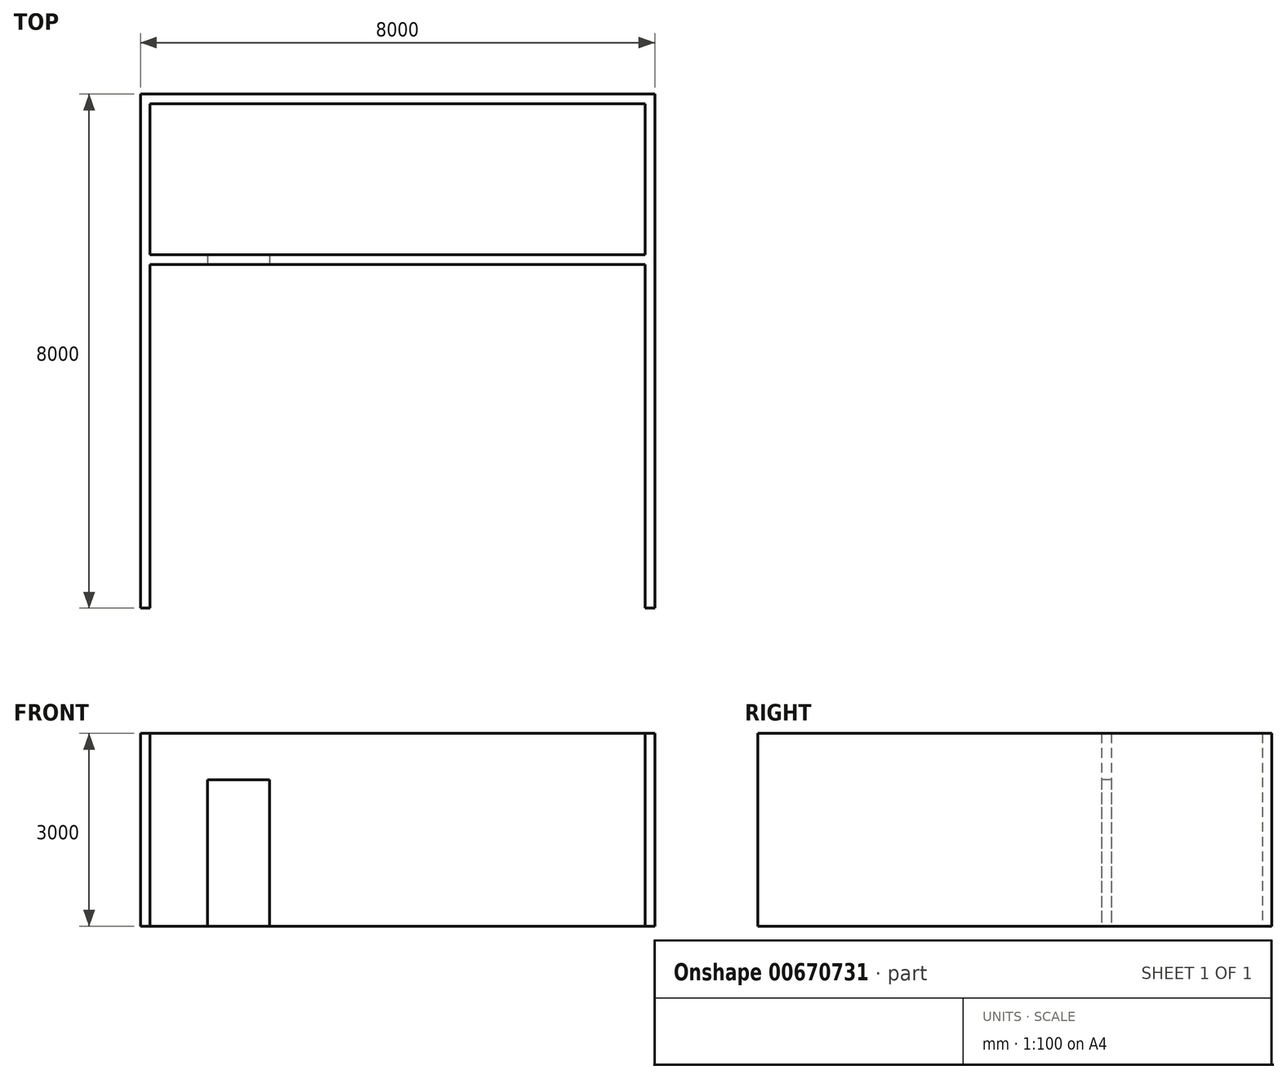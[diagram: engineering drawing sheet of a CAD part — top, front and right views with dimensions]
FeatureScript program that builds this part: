
annotation { "Feature Type Name" : "Feature", "Feature Type Description" : "" }
export const myFeature = defineFeature(function(context is Context, id is Id, definition is map)
    precondition{}
    {
        {
            var Q0;
            Q0=qCreatedBy(makeId("Top.planeOp"),FACE);
            var sketch = newSketch(context, id + "F0", { "sketchPlane" : qUnion([Q0])});
            skLineSegment(sketch, "E0.bottom", {"start": v(4000, 4000) * mm, "end": v(-4000, 4000) * mm});
            skLineSegment(sketch, "E0.top", {"start": v(4000, -4000) * mm, "end": v(3850, -4000) * mm});
            skLineSegment(sketch, "E0.left", {"start": v(4000, 4000) * mm, "end": v(4000, -4000) * mm});
            skLineSegment(sketch, "E0.right", {"start": v(-4000, 4000) * mm, "end": v(-4000, -4000) * mm});
            skPoint(sketch, "E0.middle", {"position": v(0, 0) * mm});
            skLineSegment(sketch, "E1.0", {"start": v(-3850, 3850) * mm, "end": v(-3850, -4000) * mm});
            skLineSegment(sketch, "E1.1", {"start": v(3850, 3850) * mm, "end": v(-3850, 3850) * mm});
            skLineSegment(sketch, "E1.2", {"start": v(3850, 3850) * mm, "end": v(3850, -4000) * mm});
            skLineSegment(sketch, "E2.bottom", {"start": v(-3850, 1500) * mm, "end": v(3850, 1500) * mm});
            skLineSegment(sketch, "E2.top", {"start": v(-3850, 1350) * mm, "end": v(3850, 1350) * mm});
            skLineSegment(sketch, "E2.left", {"start": v(-3850, 1500) * mm, "end": v(-3850, 1350) * mm});
            skLineSegment(sketch, "E2.right", {"start": v(3850, 1500) * mm, "end": v(3850, 1350) * mm});
            skLineSegment(sketch, "E3.trimOffspring", {"start": v(-3850, -4000) * mm, "end": v(-4000, -4000) * mm});
            skSolve(sketch);
        }
        {
            var Q0;
            Q0 = qSketchRegion(id + "F0", true);
            extrude(context, id + "F1", {"entities" : qUnion([Q0]), "depth" : 3000 * mm, "offsetDistance" : 25 * mm});
        }
        {
            var Q0;
            Q0=makeQuery(id+"F1.opExtrude","SWEPT_FACE",FACE,{"disambiguationData":[OSD([sQuery(id+"F0.wireOp",EDGE,"E2.top")])]});
            var sketch = newSketch(context, id + "F2", { "sketchPlane" : qUnion([Q0])});
            skLineSegment(sketch, "E4.bottom", {"start": v(-2955.46, 2276.68) * mm, "end": v(-1994.73, 2276.68) * mm});
            skLineSegment(sketch, "E4.top", {"start": v(-2955.46, 0) * mm, "end": v(-1994.73, 0) * mm});
            skLineSegment(sketch, "E4.left", {"start": v(-2955.46, 2276.68) * mm, "end": v(-2955.46, 0) * mm});
            skLineSegment(sketch, "E4.right", {"start": v(-1994.73, 2276.68) * mm, "end": v(-1994.73, 0) * mm});
            skSolve(sketch);
        }
        {
            var Q0;
            Q0 = qSketchRegion(id + "F2", true);
            extrude(context, id + "F3", {"entities" : qUnion([Q0]), "operationType" : NewBodyOperationType.REMOVE, "endBound" : BoundingType.UP_TO_NEXT, "oppositeDirection" : true, "depth" : 25 * mm, "offsetDistance" : 25 * mm});
        }
    });
